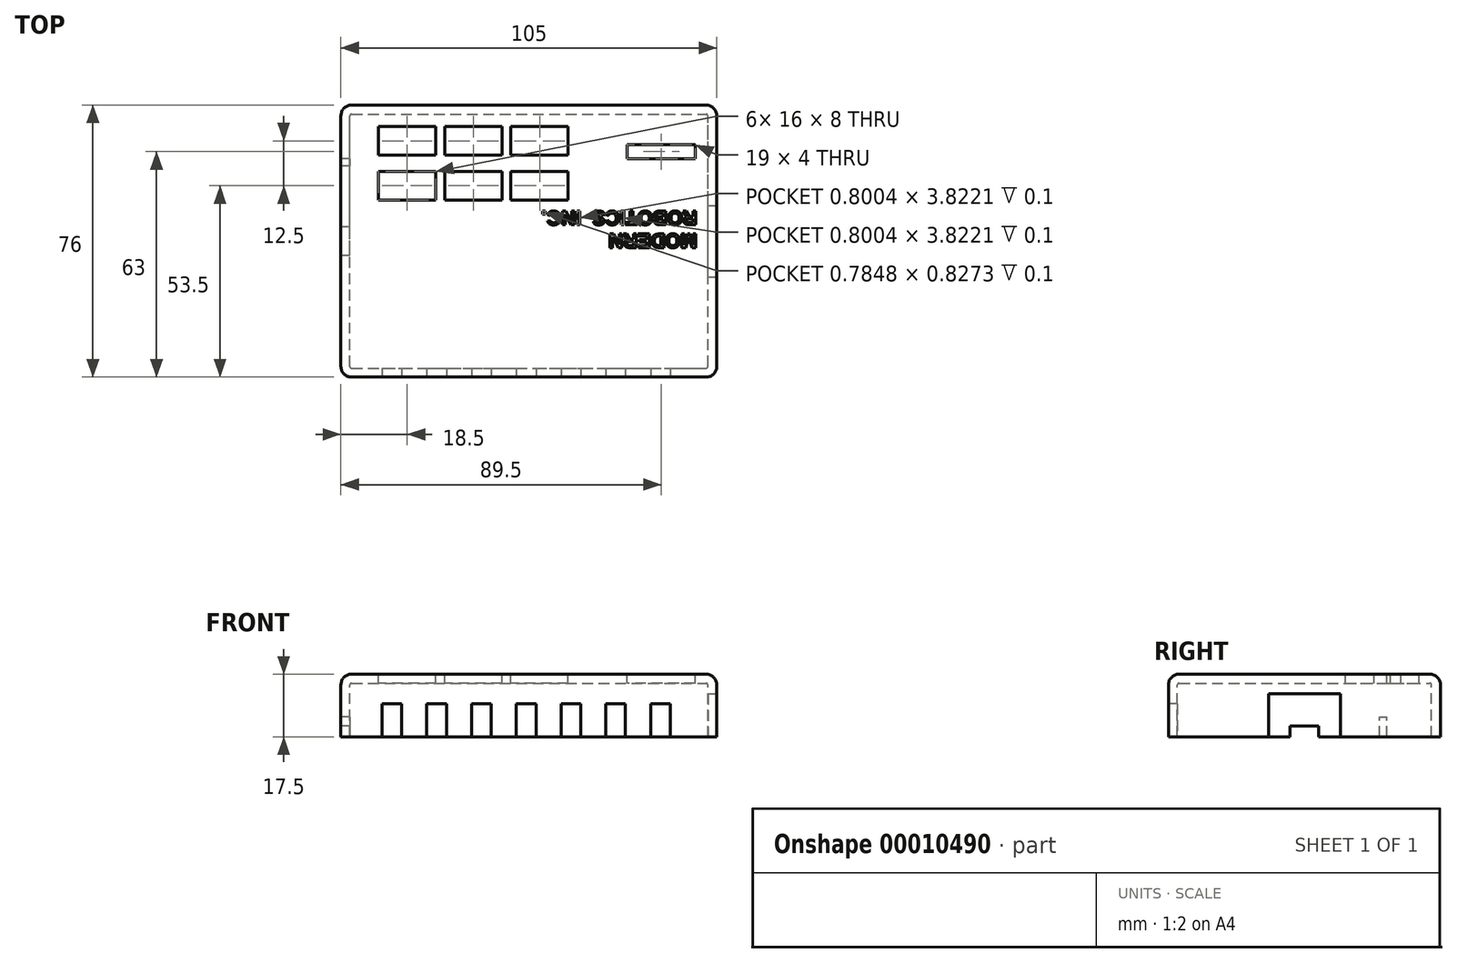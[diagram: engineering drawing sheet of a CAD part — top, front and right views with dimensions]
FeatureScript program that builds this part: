
annotation { "Feature Type Name" : "Feature", "Feature Type Description" : "" }
export const myFeature = defineFeature(function(context is Context, id is Id, definition is map)
    precondition{}
    {
        {
            var Q0;
            Q0=qCreatedBy(makeId("Top.planeOp"),FACE);
            var sketch = newSketch(context, id + "F0", { "sketchPlane" : qUnion([Q0])});
            skLineSegment(sketch, "E0.bottom", {"start": v(0, 0) * mm, "end": v(105, 0) * mm});
            skLineSegment(sketch, "E0.top", {"start": v(0, 76) * mm, "end": v(105, 76) * mm});
            skLineSegment(sketch, "E0.left", {"start": v(0, 0) * mm, "end": v(0, 76) * mm});
            skLineSegment(sketch, "E0.right", {"start": v(105, 0) * mm, "end": v(105, 76) * mm});
            skSolve(sketch);
        }
        {
            var Q0;
            Q0 = qSketchRegion(id + "F0", true);
            extrude(context, id + "F1", {"entities" : qUnion([Q0]), "depth" : 17.5 * mm});
        }
        {
            var Q0;
            Q0=makeQuery(id+"F1.opExtrude","SWEPT_EDGE",EDGE,{"disambiguationData":[OSD([sQuery(id+"F0.wireOp",EDGE,"E0.bottom"),sQuery(id+"F0.wireOp",EDGE,"E0.left")])]});
            var Q1;
            Q1=makeQuery(id+"F1.opExtrude","CAP_EDGE",EDGE,{"disambiguationData":[OSD([sQuery(id+"F0.wireOp",EDGE,"E0.bottom")])],"isStart":false});
            var Q2;
            Q2=makeQuery(id+"F1.opExtrude","CAP_EDGE",EDGE,{"disambiguationData":[OSD([sQuery(id+"F0.wireOp",EDGE,"E0.left")])],"isStart":false});
            var Q3;
            Q3=makeQuery(id+"F1.opExtrude","SWEPT_EDGE",EDGE,{"disambiguationData":[OSD([sQuery(id+"F0.wireOp",EDGE,"E0.bottom"),sQuery(id+"F0.wireOp",EDGE,"E0.right")])]});
            var Q4;
            Q4=makeQuery(id+"F1.opExtrude","CAP_EDGE",EDGE,{"disambiguationData":[OSD([sQuery(id+"F0.wireOp",EDGE,"E0.right")])],"isStart":false});
            var Q5;
            Q5=makeQuery(id+"F1.opExtrude","CAP_EDGE",EDGE,{"disambiguationData":[OSD([sQuery(id+"F0.wireOp",EDGE,"E0.top")])],"isStart":false});
            var Q6;
            Q6=makeQuery(id+"F1.opExtrude","SWEPT_EDGE",EDGE,{"disambiguationData":[OSD([sQuery(id+"F0.wireOp",EDGE,"E0.top"),sQuery(id+"F0.wireOp",EDGE,"E0.right")])]});
            var Q7;
            Q7=makeQuery(id+"F1.opExtrude","SWEPT_EDGE",EDGE,{"disambiguationData":[OSD([sQuery(id+"F0.wireOp",EDGE,"E0.top"),sQuery(id+"F0.wireOp",EDGE,"E0.left")])]});
            fillet(context, id + "F2", {"entities" : qUnion([Q0, Q1, Q2, Q3, Q4, Q5, Q6, Q7]), "radius" : 3 * mm, "tangentPropagation" : true, "allowEdgeOverflow" : false});
        }
        {
            var Q0;
            Q0=makeQuery(id+"F1.opExtrude","CAP_FACE",FACE,{"disambiguationData":[OSD([sQuery(id+"F0.wireOp",EDGE,"E0.bottom"),sQuery(id+"F0.wireOp",EDGE,"E0.top"),sQuery(id+"F0.wireOp",EDGE,"E0.left"),sQuery(id+"F0.wireOp",EDGE,"E0.right")])],"isStart":true});
            shell(context, id + "F3", {"entities" : qUnion([Q0]), "thickness" : 2.5 * mm});
        }
        {
            var Q0;
            Q0=makeQuery(id+"F1.opExtrude","CAP_FACE",FACE,{"disambiguationData":[OSD([sQuery(id+"F0.wireOp",EDGE,"E0.bottom"),sQuery(id+"F0.wireOp",EDGE,"E0.top"),sQuery(id+"F0.wireOp",EDGE,"E0.left"),sQuery(id+"F0.wireOp",EDGE,"E0.right")])],"isStart":false});
            var sketch = newSketch(context, id + "F4", { "sketchPlane" : qUnion([Q0])});
            skLineSegment(sketch, "E1.bottom", {"start": v(10.5, 70) * mm, "end": v(26.5, 70) * mm});
            skLineSegment(sketch, "E1.top", {"start": v(10.5, 62) * mm, "end": v(26.5, 62) * mm});
            skLineSegment(sketch, "E1.left", {"start": v(10.5, 70) * mm, "end": v(10.5, 62) * mm});
            skLineSegment(sketch, "E1.right", {"start": v(26.5, 70) * mm, "end": v(26.5, 62) * mm});
            skLineSegment(sketch, "E2.0.1.0", {"start": v(10.5, 49.5) * mm, "end": v(26.5, 49.5) * mm});
            skLineSegment(sketch, "E2.0.1.1", {"start": v(26.5, 57.5) * mm, "end": v(26.5, 49.5) * mm});
            skLineSegment(sketch, "E2.0.1.2", {"start": v(10.5, 57.5) * mm, "end": v(10.5, 49.5) * mm});
            skLineSegment(sketch, "E2.0.1.3", {"start": v(10.5, 57.5) * mm, "end": v(26.5, 57.5) * mm});
            skLineSegment(sketch, "E2.1.0.0", {"start": v(29, 62) * mm, "end": v(45, 62) * mm});
            skLineSegment(sketch, "E2.1.0.1", {"start": v(45, 70) * mm, "end": v(45, 62) * mm});
            skLineSegment(sketch, "E2.1.0.2", {"start": v(29, 70) * mm, "end": v(29, 62) * mm});
            skLineSegment(sketch, "E2.1.0.3", {"start": v(29, 70) * mm, "end": v(45, 70) * mm});
            skLineSegment(sketch, "E2.1.1.0", {"start": v(29, 49.5) * mm, "end": v(45, 49.5) * mm});
            skLineSegment(sketch, "E2.1.1.1", {"start": v(45, 57.5) * mm, "end": v(45, 49.5) * mm});
            skLineSegment(sketch, "E2.1.1.2", {"start": v(29, 57.5) * mm, "end": v(29, 49.5) * mm});
            skLineSegment(sketch, "E2.1.1.3", {"start": v(29, 57.5) * mm, "end": v(45, 57.5) * mm});
            skLineSegment(sketch, "E2.2.0.0", {"start": v(47.5, 62) * mm, "end": v(63.5, 62) * mm});
            skLineSegment(sketch, "E2.2.0.1", {"start": v(63.5, 70) * mm, "end": v(63.5, 62) * mm});
            skLineSegment(sketch, "E2.2.0.2", {"start": v(47.5, 70) * mm, "end": v(47.5, 62) * mm});
            skLineSegment(sketch, "E2.2.0.3", {"start": v(47.5, 70) * mm, "end": v(63.5, 70) * mm});
            skLineSegment(sketch, "E2.2.1.0", {"start": v(47.5, 49.5) * mm, "end": v(63.5, 49.5) * mm});
            skLineSegment(sketch, "E2.2.1.1", {"start": v(63.5, 57.5) * mm, "end": v(63.5, 49.5) * mm});
            skLineSegment(sketch, "E2.2.1.2", {"start": v(47.5, 57.5) * mm, "end": v(47.5, 49.5) * mm});
            skLineSegment(sketch, "E2.2.1.3", {"start": v(47.5, 57.5) * mm, "end": v(63.5, 57.5) * mm});
            skLineSegment(sketch, "E2.direction1", {"start": v(10.5, 62) * mm, "end": v(29, 62) * mm, "construction": true});
            skLineSegment(sketch, "E2.direction2", {"start": v(10.5, 62) * mm, "end": v(10.5, 49.5) * mm, "construction": true});
            skLineSegment(sketch, "E3.bottom", {"start": v(80, 65) * mm, "end": v(99, 65) * mm});
            skLineSegment(sketch, "E3.top", {"start": v(80, 61) * mm, "end": v(99, 61) * mm});
            skLineSegment(sketch, "E3.left", {"start": v(80, 65) * mm, "end": v(80, 61) * mm});
            skLineSegment(sketch, "E3.right", {"start": v(99, 65) * mm, "end": v(99, 61) * mm});
            skSolve(sketch);
        }
        {
            var Q0;
            Q0 = qSketchRegion(id + "F4", true);
            extrude(context, id + "F5", {"entities" : qUnion([Q0]), "operationType" : NewBodyOperationType.REMOVE, "endBound" : BoundingType.UP_TO_NEXT, "oppositeDirection" : true, "depth" : 25 * mm});
        }
        {
            var Q0;
            Q0=makeQuery(id+"F1.opExtrude","SWEPT_FACE",FACE,{"disambiguationData":[OSD([sQuery(id+"F0.wireOp",EDGE,"E0.bottom")])]});
            var sketch = newSketch(context, id + "F6", { "sketchPlane" : qUnion([Q0])});
            skLineSegment(sketch, "E4.bottom", {"start": v(11.5, 9.23) * mm, "end": v(17, 9.23) * mm});
            skLineSegment(sketch, "E4.top", {"start": v(11.5, 0) * mm, "end": v(17, 0) * mm});
            skLineSegment(sketch, "E4.left", {"start": v(11.5, 9.23) * mm, "end": v(11.5, 0) * mm});
            skLineSegment(sketch, "E4.right", {"start": v(17, 9.23) * mm, "end": v(17, 0) * mm});
            skLineSegment(sketch, "E5.1.0.0", {"start": v(24, 9.23) * mm, "end": v(29.5, 9.23) * mm});
            skLineSegment(sketch, "E5.1.0.1", {"start": v(24, 9.23) * mm, "end": v(24, 0) * mm});
            skLineSegment(sketch, "E5.1.0.2", {"start": v(24, 0) * mm, "end": v(29.5, 0) * mm});
            skLineSegment(sketch, "E5.1.0.3", {"start": v(29.5, 9.23) * mm, "end": v(29.5, 0) * mm});
            skLineSegment(sketch, "E5.2.0.0", {"start": v(36.5, 9.23) * mm, "end": v(42, 9.23) * mm});
            skLineSegment(sketch, "E5.2.0.1", {"start": v(36.5, 9.23) * mm, "end": v(36.5, 0) * mm});
            skLineSegment(sketch, "E5.2.0.2", {"start": v(36.5, 0) * mm, "end": v(42, 0) * mm});
            skLineSegment(sketch, "E5.2.0.3", {"start": v(42, 9.23) * mm, "end": v(42, 0) * mm});
            skLineSegment(sketch, "E5.3.0.0", {"start": v(49, 9.23) * mm, "end": v(54.5, 9.23) * mm});
            skLineSegment(sketch, "E5.3.0.1", {"start": v(49, 9.23) * mm, "end": v(49, 0) * mm});
            skLineSegment(sketch, "E5.3.0.2", {"start": v(49, 0) * mm, "end": v(54.5, 0) * mm});
            skLineSegment(sketch, "E5.3.0.3", {"start": v(54.5, 9.23) * mm, "end": v(54.5, 0) * mm});
            skLineSegment(sketch, "E5.4.0.0", {"start": v(61.5, 9.23) * mm, "end": v(67, 9.23) * mm});
            skLineSegment(sketch, "E5.4.0.1", {"start": v(61.5, 9.23) * mm, "end": v(61.5, 0) * mm});
            skLineSegment(sketch, "E5.4.0.2", {"start": v(61.5, 0) * mm, "end": v(67, 0) * mm});
            skLineSegment(sketch, "E5.4.0.3", {"start": v(67, 9.23) * mm, "end": v(67, 0) * mm});
            skLineSegment(sketch, "E5.5.0.0", {"start": v(74, 9.23) * mm, "end": v(79.5, 9.23) * mm});
            skLineSegment(sketch, "E5.5.0.1", {"start": v(74, 9.23) * mm, "end": v(74, 0) * mm});
            skLineSegment(sketch, "E5.5.0.2", {"start": v(74, 0) * mm, "end": v(79.5, 0) * mm});
            skLineSegment(sketch, "E5.5.0.3", {"start": v(79.5, 9.23) * mm, "end": v(79.5, 0) * mm});
            skLineSegment(sketch, "E5.6.0.0", {"start": v(86.5, 9.23) * mm, "end": v(92, 9.23) * mm});
            skLineSegment(sketch, "E5.6.0.1", {"start": v(86.5, 9.23) * mm, "end": v(86.5, 0) * mm});
            skLineSegment(sketch, "E5.6.0.2", {"start": v(86.5, 0) * mm, "end": v(92, 0) * mm});
            skLineSegment(sketch, "E5.6.0.3", {"start": v(92, 9.23) * mm, "end": v(92, 0) * mm});
            skLineSegment(sketch, "E5.direction1", {"start": v(11, 9.23) * mm, "end": v(23.5, 9.23) * mm, "construction": true});
            skSolve(sketch);
        }
        {
            var Q0;
            Q0 = qSketchRegion(id + "F6", true);
            extrude(context, id + "F7", {"entities" : qUnion([Q0]), "operationType" : NewBodyOperationType.REMOVE, "endBound" : BoundingType.UP_TO_NEXT, "oppositeDirection" : true, "depth" : 25 * mm});
        }
        {
            var Q0;
            Q0=makeQuery(id+"F1.opExtrude","SWEPT_FACE",FACE,{"disambiguationData":[OSD([sQuery(id+"F0.wireOp",EDGE,"E0.right")])]});
            var sketch = newSketch(context, id + "F8", { "sketchPlane" : qUnion([Q0])});
            skLineSegment(sketch, "E6.bottom", {"start": v(28, 12) * mm, "end": v(48, 12) * mm});
            skLineSegment(sketch, "E6.top", {"start": v(28, 0) * mm, "end": v(48, 0) * mm});
            skLineSegment(sketch, "E6.left", {"start": v(28, 12) * mm, "end": v(28, 0) * mm});
            skLineSegment(sketch, "E6.right", {"start": v(48, 12) * mm, "end": v(48, 0) * mm});
            skPoint(sketch, "E7", {"position": v(38, 0) * mm});
            skPoint(sketch, "E8", {"position": v(100.9, 31.9) * mm});
            skSolve(sketch);
        }
        {
            var Q0;
            Q0 = qSketchRegion(id + "F8", true);
            extrude(context, id + "F9", {"entities" : qUnion([Q0]), "operationType" : NewBodyOperationType.REMOVE, "endBound" : BoundingType.UP_TO_NEXT, "oppositeDirection" : true, "depth" : 25 * mm});
        }
        {
            var Q0;
            Q0=makeQuery(id+"F1.opExtrude","SWEPT_FACE",FACE,{"disambiguationData":[OSD([sQuery(id+"F0.wireOp",EDGE,"E0.left")])]});
            var sketch = newSketch(context, id + "F10", { "sketchPlane" : qUnion([Q0])});
            skLineSegment(sketch, "E9.bottom", {"start": v(-59, 0) * mm, "end": v(-61, 0) * mm});
            skLineSegment(sketch, "E9.top", {"start": v(-59, 5.5) * mm, "end": v(-61, 5.5) * mm});
            skLineSegment(sketch, "E9.left", {"start": v(-59, 0) * mm, "end": v(-59, 5.5) * mm});
            skLineSegment(sketch, "E9.right", {"start": v(-61, 0) * mm, "end": v(-61, 5.5) * mm});
            skLineSegment(sketch, "E10.bottom", {"start": v(-42, 0) * mm, "end": v(-34, 0) * mm});
            skLineSegment(sketch, "E10.top", {"start": v(-42, 3) * mm, "end": v(-34, 3) * mm});
            skLineSegment(sketch, "E10.left", {"start": v(-42, 0) * mm, "end": v(-42, 3) * mm});
            skLineSegment(sketch, "E10.right", {"start": v(-34, 0) * mm, "end": v(-34, 3) * mm});
            skPoint(sketch, "E11", {"position": v(-38, 0) * mm});
            skSolve(sketch);
        }
        {
            var Q0;
            Q0 = qSketchRegion(id + "F10", true);
            extrude(context, id + "F11", {"entities" : qUnion([Q0]), "operationType" : NewBodyOperationType.REMOVE, "endBound" : BoundingType.UP_TO_NEXT, "oppositeDirection" : true, "depth" : 25 * mm});
        }
        {
            var Q0;
            Q0=makeQuery(id+"F4.imprint","IMPRINT",FACE,{"disambiguationData":[TD([[makeQuery(id+"F4.imprint","IMPRINT",EDGE,{"derivedFrom":sQuery(id+"F4.wireOp",EDGE,"E1.bottom")}),1.0]])]});
            var sketch = newSketch(context, id + "F12", { "sketchPlane" : qUnion([Q0])});
            skText(sketch, "E12", { "text": "MODERN\nROBOTICS  INC.", "fontName": "Arimo-Bold.ttf"});
            const initialGuessF12  = {"E12": [0.0995, 0.04, -1, 0, 0.004]};
            skSetInitialGuess(sketch, initialGuessF12);
            skSolve(sketch);
        }
        {
            var Q0;
            Q0 = qSketchRegion(id + "F12", true);
            extrude(context, id + "F13", {"entities" : qUnion([Q0]), "operationType" : NewBodyOperationType.REMOVE, "oppositeDirection" : true, "depth" : .1 * mm});
        }
    });
